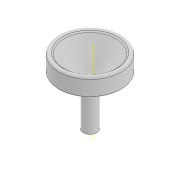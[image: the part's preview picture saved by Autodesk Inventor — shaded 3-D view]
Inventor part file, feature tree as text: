
AUTODESK INVENTOR PART (.ipt)
format: ipt  version: 2022 (Build 260153000, 153)  size: 191,488 bytes
history: native  units: mm
features: revolve x2, other x2, sketch x1
ambient origin geometry x8: Origin, YZ Plane, XZ Plane, XY Plane, X Axis, Y Axis, Z Axis, Center Point
bodies: Solid1 (feature_tree)
feature tree (5):
  revolve  "Revolution1"  [1 undecoded]
  sketch  "Sketch2"  dims[d0=4.44mm d1=44.0mm d2=4.49mm d5=9.22mm d6=17.894861mm d7=4.9mm d8=5.42mm d9=11.833332mm d10=1.0mm d11=90.0deg d14=4.84mm d16=17.42mm d18=4.41mm d19=5.0mm d20=5.3mm d21=6.63mm d22=1.0mm d23=1.0mm d24=90.0deg]
  other  "Work Axis2"
  revolve  "Revolution2"  [1 undecoded]
  other  "Work Axis1"
note: 2 required parameter values undecoded (feature->parameter linkage not recoverable at this tier; creation-order binding heuristic only, values carry confidence <= 0.55)
